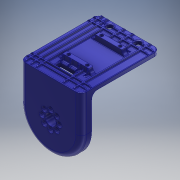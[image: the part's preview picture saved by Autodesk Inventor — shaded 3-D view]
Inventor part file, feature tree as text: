
AUTODESK INVENTOR PART (.ipt)
format: ipt  version: 2018 (Build 220112000, 112)  size: 4,532,736 bytes
history: native  units: mm
features: projected_geometry x13, fillet x12, sketch x12, extrude x6, hole x3, rib x2, pattern_linear x2, plane x1, mirror x1
ambient origin geometry x8: Origin, YZ Plane, XZ Plane, XY Plane, X Axis, Y Axis, Z Axis, Center Point
bodies: Solid1 (feature_tree)
feature tree (52):
  extrude  "Extrusion1"  Depth=28.0mm
  extrude  "Extrusion2"  TaperAngle=90.0deg  [1 undecoded]
  hole  "Hole1"  [1 undecoded]
  extrude  "Extrusion3"  Depth=4.0mm
  extrude  "Extrusion4"  TaperAngle=90.0deg  [1 undecoded]
  extrude  "Extrusion5"  Depth=6.0mm
  hole  "Hole2"  [1 undecoded]
  fillet  "Fillet3"  Radius=24.0mm
  fillet  "Fillet4"  Radius=4.0mm
  fillet  "Fillet5"  Radius=24.0mm
  hole  "Hole3"  [1 undecoded]
  sketch  "Sketch10"  dims[d51=10.0mm]
  rib  "Rib2"
  plane  "Work Plane1"
  pattern_linear  "Rectangular Pattern3"  Spacing1=1.0mm  [1 undecoded]
  pattern_linear  "Rectangular Pattern4"  Spacing1=1.0mm  [1 undecoded]
  mirror  "Mirror1"
  fillet  "Fillet6"  Radius=5.0mm
  fillet  "Fillet7"  Radius=1.0mm
  fillet  "Fillet8"  Radius=30.0mm
  fillet  "Fillet9"  Radius=20.0mm
  rib  "Rib3"
  fillet  "Fillet10"  Radius=1.0mm
  fillet  "Fillet11"  Radius=1.0mm
  extrude  "Extrusion6"  Depth=0.5mm
  fillet  "Fillet12"  Radius=0.5mm
  fillet  "Fillet13"  Radius=5.0mm
  fillet  "Fillet14"  Radius=5.0mm
  sketch  "Sketch1"  dims[d1=80.0mm d2=1.0mm d3=10.0mm d4=16.0mm d5=2.9mm d6=360.0deg d7=28.0mm]
  sketch  "Sketch2"  dims[d8=34.0mm d9=90.0deg]
  projected_geometry  "Projected Loop1"
  sketch  "Sketch3"  dims[d10=10.0mm d11=0.0mm d12=4.5mm d13=0.0mm]
  projected_geometry  "Projected Loop2"
  sketch  "Sketch4"  dims[d14=5.0mm d15=6.0mm d16=4.0mm d17=2.0mm d18=90.0deg d19=10.5mm d20=0.0mm d21=4.0mm]
  sketch  "Sketch5"  dims[d22=62.0mm d23=0.0mm d24=90.0deg]
  projected_geometry  "Projected Loop3"
  sketch  "Sketch7"  dims[d25=15.0mm d26=6.0mm]
  projected_geometry  "Projected Loop5"
  sketch  "Sketch8"  dims[d27=52.0mm d28=0.0mm d44=72.0mm d45=24.0mm d46=4.0mm d47=24.0mm]
  sketch  "Sketch9"  dims[d48=4.0mm d49=5.0mm d50=0.0mm]
  projected_geometry  "Projected Loop6"
  projected_geometry  "Projected Loop7"
  projected_geometry  "Projected Loop8"
  projected_geometry  "Projected Loop9"
  projected_geometry  "Projected Loop10"
  sketch  "Sketch11"  dims[d52=15.0mm]
  projected_geometry  "Projected Loop11"
  projected_geometry  "Projected Loop12"
  sketch  "Sketch12"  dims[d53=15.0mm]
  projected_geometry  "Projected Loop13"
  sketch  "Sketch13"  dims[d54=5.2mm d55=6.0mm d56=4.0mm d57=2.0mm d58=90.0deg d59=10.5mm d60=0.0mm d61=1.0mm d62=1.0mm d63=5.0mm d64=3.0mm d65=6.0mm d66=5.0mm d67=3.0mm d68=90.0deg d69=3.0mm d70=0.0mm d71=1.0mm d72=1.0mm d73=0.0mm d74=0.0mm d75=1.0mm d76=1.0mm d77=30.0mm d79=7.5mm d80=20.0mm d82=15.5mm d83=1.0mm d84=1.0mm d85=0.5mm d86=0.5mm d87=5.0mm d88=5.0mm d89=1.0mm d90=1.5mm d91=0.0mm d92=0.0mm d93=1.0mm d94=1.0mm d95=2.0mm d96=0.5mm d97=2.0mm d98=0.0mm d99=0.5mm d100=0.5mm d101=0.5mm]
  projected_geometry  "Projected Loop14"
note: 7 required parameter values undecoded (feature->parameter linkage not recoverable at this tier; creation-order binding heuristic only, values carry confidence <= 0.55)
